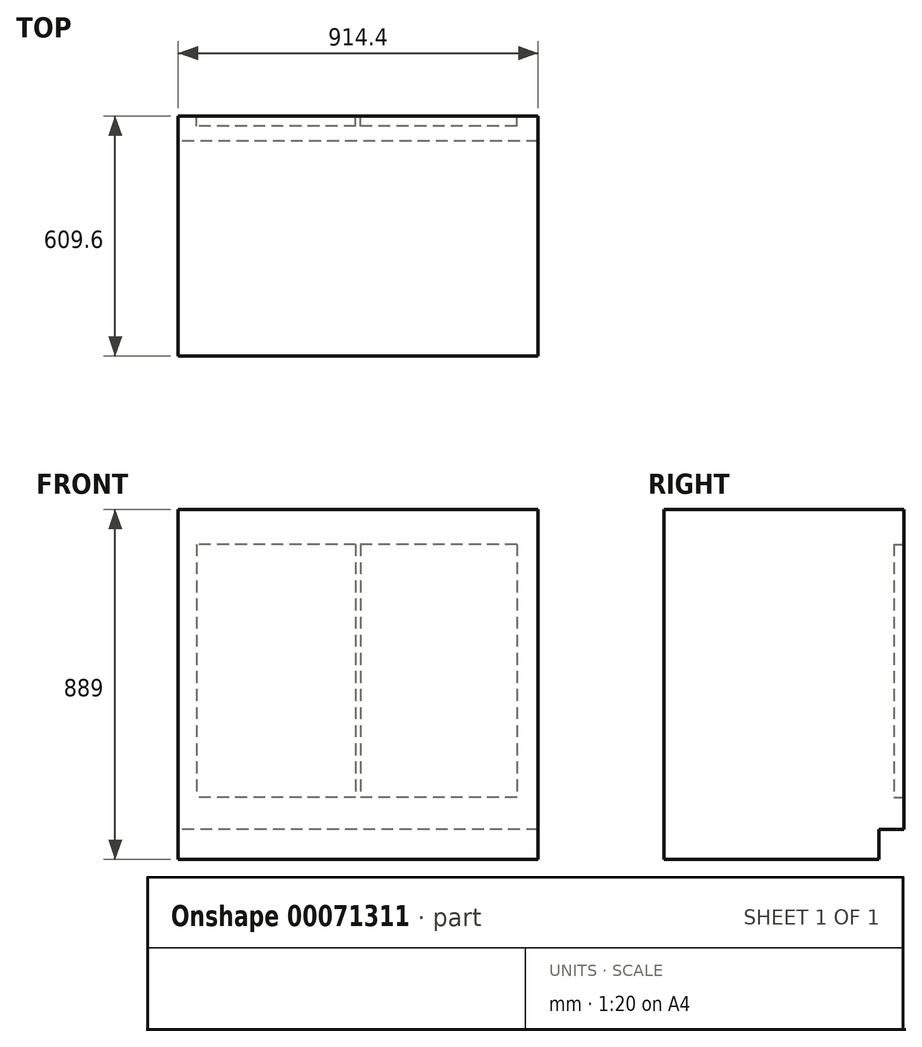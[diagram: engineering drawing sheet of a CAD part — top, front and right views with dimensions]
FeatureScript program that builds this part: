
annotation { "Feature Type Name" : "Feature", "Feature Type Description" : "" }
export const myFeature = defineFeature(function(context is Context, id is Id, definition is map)
    precondition{}
    {
        {
            var Q0;
            Q0=qCreatedBy(makeId("Top.planeOp"),FACE);
            var sketch = newSketch(context, id + "F0", { "sketchPlane" : qUnion([Q0])});
            skLineSegment(sketch, "E0.rect.bottom", {"start": v(457.2, 304.8) * mm, "end": v(-457.2, 304.8) * mm});
            skLineSegment(sketch, "E0.rect.top", {"start": v(457.2, -304.8) * mm, "end": v(-457.2, -304.8) * mm});
            skLineSegment(sketch, "E0.rect.left", {"start": v(457.2, 304.8) * mm, "end": v(457.2, -304.8) * mm});
            skLineSegment(sketch, "E0.rect.right", {"start": v(-457.2, 304.8) * mm, "end": v(-457.2, -304.8) * mm});
            skPoint(sketch, "E0.rect.middle", {"position": v(0, 0) * mm});
            skSolve(sketch);
        }
        {
            var Q0;
            Q0 = qSketchRegion(id + "F0", true);
            extrude(context, id + "F1", {"entities" : qUnion([Q0]), "depth" : 889 * mm});
        }
        {
            var Q0;
            Q0=makeQuery(id+"F1.opExtrude","SWEPT_FACE",FACE,{"disambiguationData":[OSD([sQuery(id+"F0.wireOp",EDGE,"E0.rect.right")])]});
            var sketch = newSketch(context, id + "F2", { "sketchPlane" : qUnion([Q0])});
            skLineSegment(sketch, "E1.bottom", {"start": v(-304.8, 0) * mm, "end": v(-241.3, 0) * mm});
            skLineSegment(sketch, "E1.top", {"start": v(-304.8, 76.2) * mm, "end": v(-241.3, 76.2) * mm});
            skLineSegment(sketch, "E1.left", {"start": v(-304.8, 0) * mm, "end": v(-304.8, 76.2) * mm});
            skLineSegment(sketch, "E1.right", {"start": v(-241.3, 0) * mm, "end": v(-241.3, 76.2) * mm});
            skSolve(sketch);
        }
        {
            var Q0;
            Q0 = qSketchRegion(id + "F2", true);
            extrude(context, id + "F3", {"entities" : qUnion([Q0]), "operationType" : NewBodyOperationType.REMOVE, "oppositeDirection" : true, "depth" : 914.4 * mm});
        }
        {
            var Q0;
            Q0=makeQuery(id+"F1.opExtrude","SWEPT_FACE",FACE,{"disambiguationData":[OSD([sQuery(id+"F0.wireOp",EDGE,"E0.rect.bottom")])]});
            var sketch = newSketch(context, id + "F4", { "sketchPlane" : qUnion([Q0])});
            skLineSegment(sketch, "E2.bottom", {"start": v(-403.53, 800.63) * mm, "end": v(-6.35, 800.63) * mm});
            skLineSegment(sketch, "E2.top", {"start": v(-403.53, 158.21) * mm, "end": v(-6.35, 158.21) * mm});
            skLineSegment(sketch, "E2.left", {"start": v(-403.53, 800.63) * mm, "end": v(-403.53, 158.21) * mm});
            skLineSegment(sketch, "E2.right", {"start": v(410.4, 800.63) * mm, "end": v(410.4, 158.21) * mm});
            skLineSegment(sketch, "E3.0", {"start": v(-6.35, 800.63) * mm, "end": v(-6.35, 158.21) * mm});
            skLineSegment(sketch, "E4.0", {"start": v(6.35, 800.63) * mm, "end": v(6.35, 158.21) * mm});
            skLineSegment(sketch, "E5.trimOffspring", {"start": v(6.35, 800.63) * mm, "end": v(410.4, 800.63) * mm});
            skLineSegment(sketch, "E6.trimOffspring", {"start": v(6.35, 158.21) * mm, "end": v(410.4, 158.21) * mm});
            skSolve(sketch);
        }
        {
            var Q0;
            Q0 = qSketchRegion(id + "F4", true);
            extrude(context, id + "F5", {"entities" : qUnion([Q0]), "operationType" : NewBodyOperationType.REMOVE, "oppositeDirection" : true, "depth" : 25.4 * mm});
        }
    });
